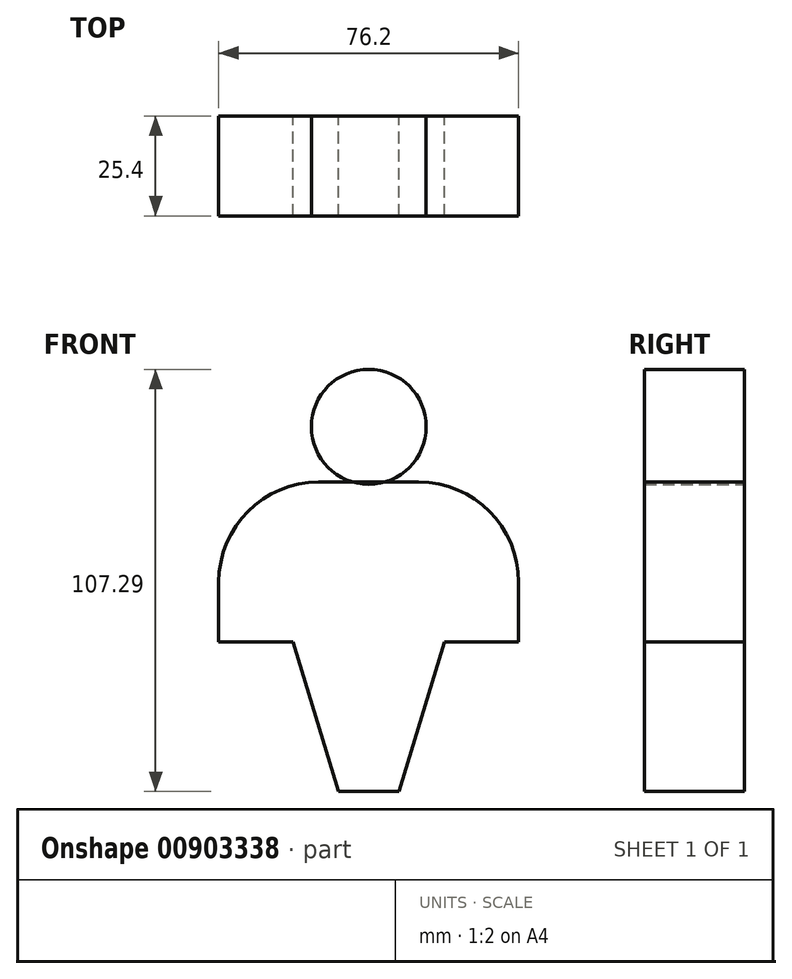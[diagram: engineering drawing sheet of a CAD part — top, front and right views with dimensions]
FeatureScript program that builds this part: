
annotation { "Feature Type Name" : "Feature", "Feature Type Description" : "" }
export const myFeature = defineFeature(function(context is Context, id is Id, definition is map)
    precondition{}
    {
        {
            var Q0;
            Q0=qCreatedBy(makeId("Front.planeOp"),FACE);
            var sketch = newSketch(context, id + "F0", { "sketchPlane" : qUnion([Q0])});
            skLineSegment(sketch, "E0.bottom", {"start": v(0, 34.43) * mm, "end": v(12.7, 34.43) * mm});
            skLineSegment(sketch, "E0.top", {"start": v(0, -6.21) * mm, "end": v(38.1, -6.21) * mm});
            skLineSegment(sketch, "E0.left", {"start": v(0, 34.43) * mm, "end": v(0, -6.21) * mm});
            skLineSegment(sketch, "E0.right", {"start": v(38.1, 9.03) * mm, "end": v(38.1, -6.21) * mm});
            skLineSegment(sketch, "E1.MirrorCS", {"start": v(-38.1, 9.03) * mm, "end": v(-38.1, -6.21) * mm});
            skLineSegment(sketch, "E2.MirrorCS", {"start": v(0, -6.21) * mm, "end": v(-38.1, -6.21) * mm});
            skLineSegment(sketch, "E3.MirrorCS", {"start": v(0, 34.43) * mm, "end": v(-12.7, 34.43) * mm});
            skPoint(sketch, "E4.visualSharp", {"position": v(-38.1, 34.43) * mm});
            skArc(sketch, "E4.filletArc", {"start": v(-12.7, 34.43) * mm, "mid": v(-30.66, 26.99) * mm, "end": v(-38.1, 9.03) * mm});
            skPoint(sketch, "E5.visualSharp", {"position": v(38.1, 34.43) * mm});
            skArc(sketch, "E5.filletArc", {"start": v(38.1, 9.03) * mm, "mid": v(30.66, 26.99) * mm, "end": v(12.7, 34.43) * mm});
            skLineSegment(sketch, "E6.bottom", {"start": v(-19.25, -6.21) * mm, "end": v(0, -5.86) * mm});
            skLineSegment(sketch, "E6.left", {"start": v(-19.25, -6.21) * mm, "end": v(-7.64, -44.21) * mm});
            skLineSegment(sketch, "E6.right", {"start": v(0, -5.86) * mm, "end": v(0, -5.86) * mm});
            skLineSegment(sketch, "E7.MirrorCS", {"start": v(19.25, -6.21) * mm, "end": v(7.64, -44.21) * mm});
            skLineSegment(sketch, "E8", {"start": v(-7.64, -44.21) * mm, "end": v(7.64, -44.21) * mm});
            skSolve(sketch);
        }
        {
            var Q0;
            Q0=qCreatedBy(makeId("Front.planeOp"),FACE);
            var sketch = newSketch(context, id + "F1", { "sketchPlane" : qUnion([Q0])});
            skCircle(sketch, "E9", {"center": v(0, 48.47) * mm, "radius": 14.6 * mm});
            skSolve(sketch);
        }
        {
            var Q0;
            Q0=qSketchRegion(id+"F0",true);
            extrude(context, id + "F2", {"entities" : qUnion([Q0]), "depth" : 12.7 * mm, "offsetDistance" : 25.4 * mm, "hasSecondDirection" : true, "secondDirectionOppositeDirection" : true, "secondDirectionDepth" : 12.7 * mm});
        }
        {
            var Q0;
            Q0=makeQuery(id+"F1.imprint","IMPRINT",FACE,{"disambiguationData":[TD([[makeQuery(id+"F1.imprint","IMPRINT",EDGE,{"derivedFrom":sQuery(id+"F1.wireOp",EDGE,"E9")}),1.0]])]});
            var Q1;
            Q1=sQuery(id+"F1.wireOp",EDGE,"E9");
            extrude(context, id + "F3", {"entities" : qUnion([Q0]), "surfaceEntities" : qUnion([Q1]), "depth" : 12.7 * mm, "offsetDistance" : 25.4 * mm, "hasSecondDirection" : true, "secondDirectionOppositeDirection" : true, "secondDirectionDepth" : 12.7 * mm});
        }
    });
